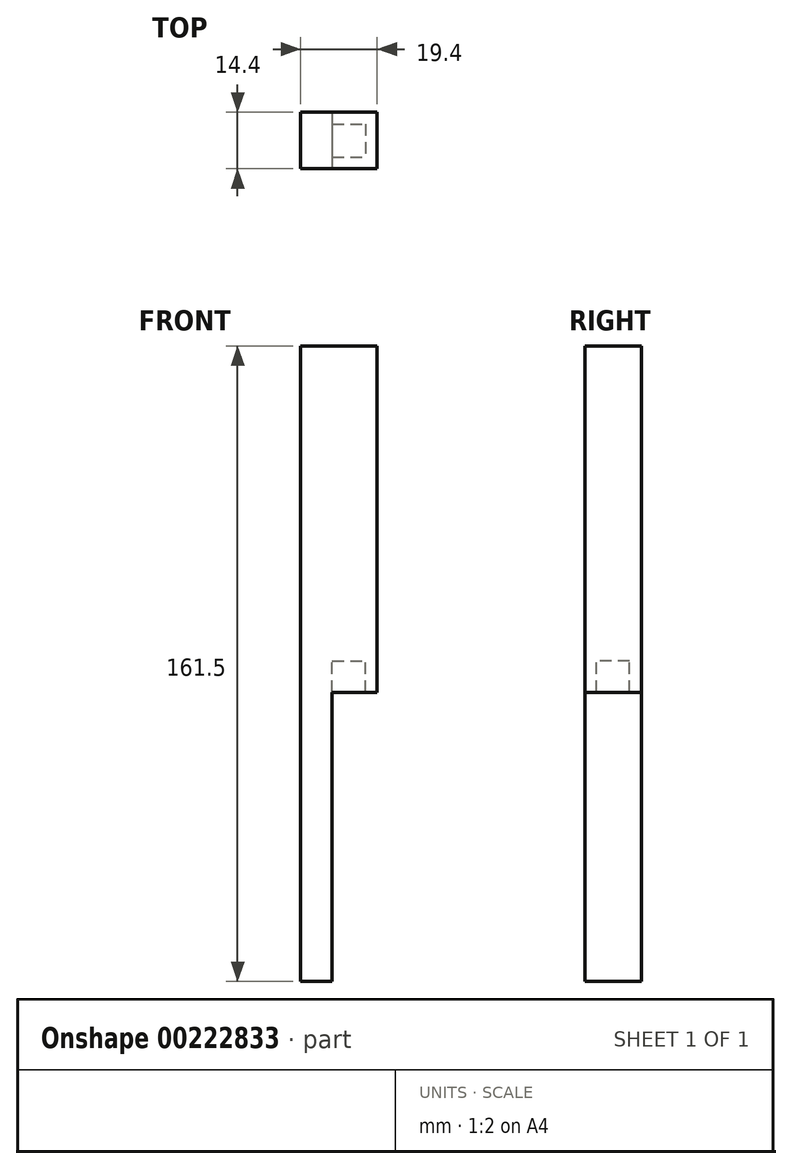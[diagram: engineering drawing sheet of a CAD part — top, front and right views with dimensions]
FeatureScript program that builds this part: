
annotation { "Feature Type Name" : "Feature", "Feature Type Description" : "" }
export const myFeature = defineFeature(function(context is Context, id is Id, definition is map)
    precondition{}
    {
        {
            var Q0;
            Q0=qCreatedBy(makeId("Top.planeOp"),FACE);
            var sketch = newSketch(context, id + "F0", { "sketchPlane" : qUnion([Q0])});
            skLineSegment(sketch, "E0.bottom", {"start": v(-4.2, 4.2) * mm, "end": v(4.2, 4.2) * mm});
            skLineSegment(sketch, "E0.top", {"start": v(-4.2, -4.2) * mm, "end": v(4.2, -4.2) * mm});
            skLineSegment(sketch, "E0.left", {"start": v(-4.2, 4.2) * mm, "end": v(-4.2, -4.2) * mm});
            skLineSegment(sketch, "E0.right", {"start": v(4.2, 4.2) * mm, "end": v(4.2, -4.2) * mm});
            skLineSegment(sketch, "E1.0", {"start": v(-7.2, 7.2) * mm, "end": v(7.2, 7.2) * mm});
            skLineSegment(sketch, "E1.1", {"start": v(-7.2, 7.2) * mm, "end": v(-7.2, -7.2) * mm});
            skLineSegment(sketch, "E1.2", {"start": v(-7.2, -7.2) * mm, "end": v(7.2, -7.2) * mm});
            skLineSegment(sketch, "E1.3", {"start": v(7.2, 7.2) * mm, "end": v(7.2, -7.2) * mm});
            skLineSegment(sketch, "E2.bottom", {"start": v(-7.2, 7.2) * mm, "end": v(-12.2, 7.2) * mm});
            skLineSegment(sketch, "E2.top", {"start": v(-7.2, -7.2) * mm, "end": v(-12.2, -7.2) * mm});
            skLineSegment(sketch, "E2.right", {"start": v(-12.2, 7.2) * mm, "end": v(-12.2, -7.2) * mm});
            skLineSegment(sketch, "E3.bottom", {"start": v(-12.2, 7.2) * mm, "end": v(-4.2, 7.2) * mm});
            skLineSegment(sketch, "E3.top", {"start": v(-12.2, -7.2) * mm, "end": v(-4.2, -7.2) * mm});
            skLineSegment(sketch, "E3.right", {"start": v(-4.2, 7.2) * mm, "end": v(-4.2, -7.2) * mm});
            skSolve(sketch);
        }
        {
            var Q0;
            {var subQ6=sQuery(id+"F0.wireOp",EDGE,"E1.1");Q0=makeQuery(id+"F0.imprint","IMPRINT",FACE,{"disambiguationData":[TD([[makeQuery(id+"F0.imprint","IMPRINT",EDGE,{"derivedFrom":subQ6}),1.0]])]});}
            var Q1;
            {var subQ0=sQuery(id+"F0.wireOp",EDGE,"E1.1");Q1=makeQuery(id+"F0.imprint","IMPRINT",FACE,{"disambiguationData":[TD([[makeQuery(id+"F0.imprint","IMPRINT",EDGE,{"derivedFrom":subQ0}),-1.0]])]});}
            extrude(context, id + "F1", {"entities" : qUnion([Q0, Q1]), "oppositeDirection" : true, "depth" : 81.5 * mm});
        }
        {
            var Q0;
            {var subQ2=sQuery(id+"F0.wireOp",EDGE,"E0.bottom");Q0=makeQuery(id+"F0.imprint","IMPRINT",FACE,{"disambiguationData":[TD([[makeQuery(id+"F0.imprint","IMPRINT",EDGE,{"derivedFrom":subQ2}),1.0]])]});}
            extrude(context, id + "F2", {"entities" : qUnion([Q0]), "operationType" : NewBodyOperationType.ADD, "oppositeDirection" : true, "depth" : 8 * mm});
        }
        {
            var Q0;
            {var subQ0=sQuery(id+"F0.wireOp",EDGE,"E1.1");Q0=makeQuery(id+"F0.imprint","IMPRINT",FACE,{"disambiguationData":[TD([[makeQuery(id+"F0.imprint","IMPRINT",EDGE,{"derivedFrom":subQ0}),-1.0]])]});}
            var Q1;
            {var subQ6=sQuery(id+"F0.wireOp",EDGE,"E1.1");Q1=makeQuery(id+"F0.imprint","IMPRINT",FACE,{"disambiguationData":[TD([[makeQuery(id+"F0.imprint","IMPRINT",EDGE,{"derivedFrom":subQ6}),1.0]])]});}
            var Q2;
            {var subQ2=sQuery(id+"F0.wireOp",EDGE,"E0.bottom");Q2=makeQuery(id+"F0.imprint","IMPRINT",FACE,{"disambiguationData":[TD([[makeQuery(id+"F0.imprint","IMPRINT",EDGE,{"derivedFrom":subQ2}),1.0]])]});}
            extrude(context, id + "F3", {"entities" : qUnion([Q0, Q1, Q2]), "operationType" : NewBodyOperationType.ADD, "depth" : 80 * mm});
        }
        {
            var Q0;
            Q0=makeQuery(id+"F3.opExtrude","CAP_FACE",FACE,{"disambiguationData":[OSD([sQuery(id+"F0.wireOp",EDGE,"E0.bottom"),sQuery(id+"F0.wireOp",EDGE,"E0.top"),sQuery(id+"F0.wireOp",EDGE,"E0.right"),sQuery(id+"F0.wireOp",EDGE,"E1.0"),sQuery(id+"F0.wireOp",EDGE,"E1.2"),sQuery(id+"F0.wireOp",EDGE,"E1.3"),sQuery(id+"F0.wireOp",EDGE,"E3.bottom"),sQuery(id+"F0.wireOp",EDGE,"E3.top"),sQuery(id+"F0.wireOp",EDGE,"E2.right"),sQuery(id+"F0.wireOp",EDGE,"E3.right")])],"isStart":false});
            var sketch = newSketch(context, id + "F4", { "sketchPlane" : qUnion([Q0])});
            skLineSegment(sketch, "E4.bottom", {"start": v(-4.2, 4.2) * mm, "end": v(4.2, 4.2) * mm});
            skLineSegment(sketch, "E4.top", {"start": v(-4.2, -4.2) * mm, "end": v(4.2, -4.2) * mm});
            skLineSegment(sketch, "E4.left", {"start": v(-4.2, 4.2) * mm, "end": v(-4.2, -4.2) * mm});
            skLineSegment(sketch, "E4.right", {"start": v(4.2, 4.2) * mm, "end": v(4.2, -4.2) * mm});
            skSolve(sketch);
        }
        {
            var Q0;
            Q0=makeQuery(id+"F4.imprint","IMPRINT",FACE,{"disambiguationData":[TD([[makeQuery(id+"F4.imprint","IMPRINT",EDGE,{"derivedFrom":sQuery(id+"F4.wireOp",EDGE,"E4.bottom")}),-1.0]])]});
            extrude(context, id + "F5", {"entities" : qUnion([Q0]), "operationType" : NewBodyOperationType.ADD, "oppositeDirection" : true, "depth" : 80 * mm});
        }
    });
